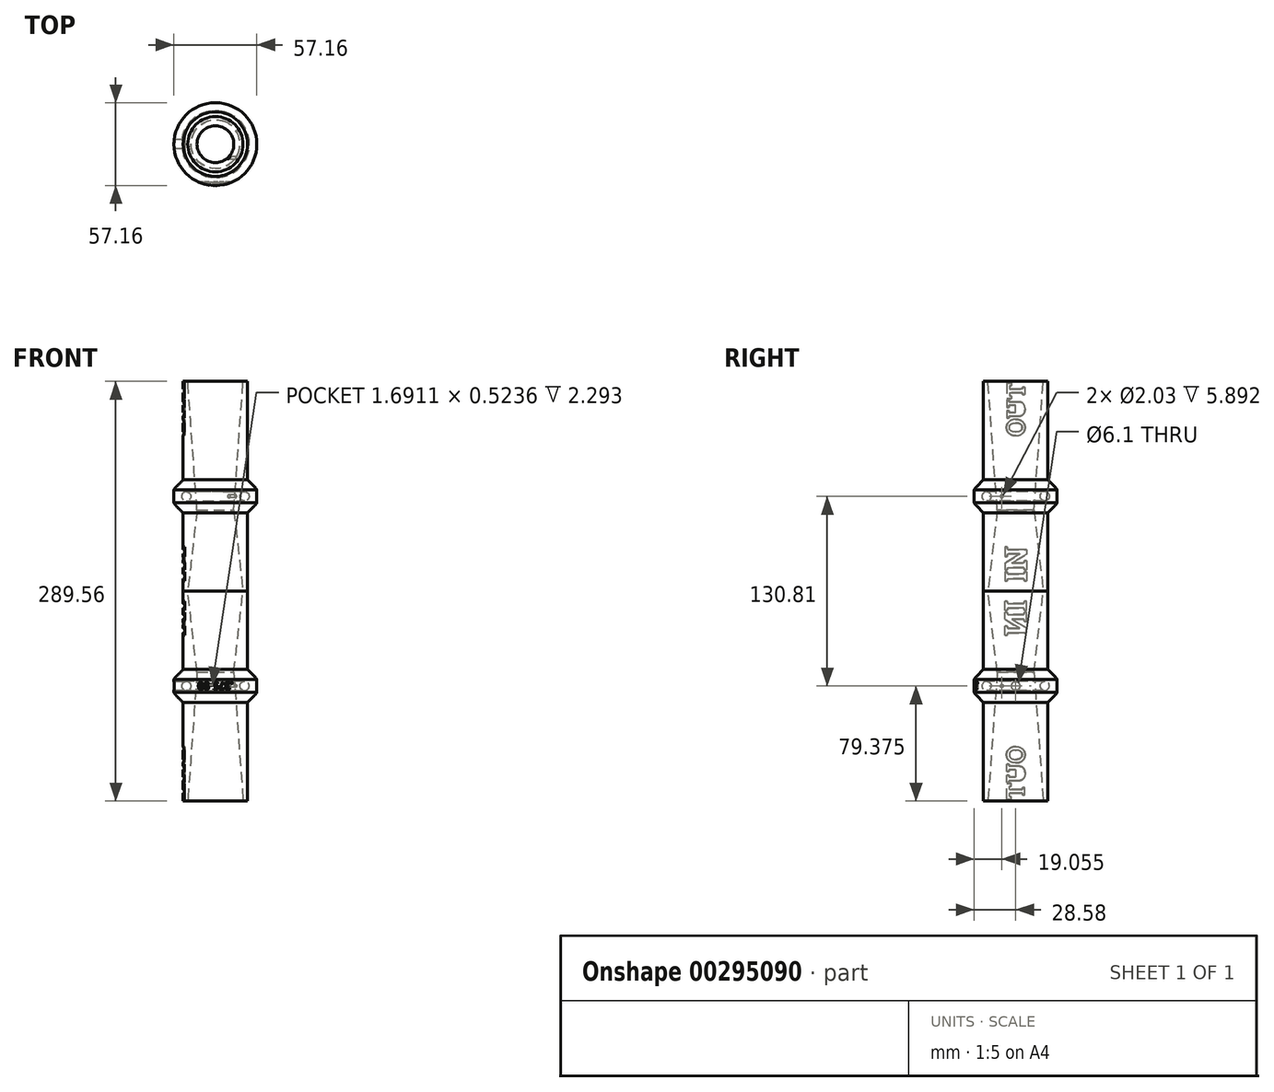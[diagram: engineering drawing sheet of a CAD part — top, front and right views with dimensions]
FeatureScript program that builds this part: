
annotation { "Feature Type Name" : "Feature", "Feature Type Description" : "" }
export const myFeature = defineFeature(function(context is Context, id is Id, definition is map)
    precondition{}
    {
        {
            var Q0;
            Q0=qCreatedBy(makeId("Front.planeOp"),FACE);
            var sketch = newSketch(context, id + "F0", { "sketchPlane" : qUnion([Q0])});
            skLineSegment(sketch, "E0", {"start": v(0, 0) * mm, "end": v(0, 144.78) * mm, "construction": true});
            skLineSegment(sketch, "E1", {"start": v(-19.05, 144.78) * mm, "end": v(-22.23, 144.78) * mm});
            skLineSegment(sketch, "E2", {"start": v(-22.23, 144.78) * mm, "end": v(-22.22, 106.68) * mm});
            skLineSegment(sketch, "E3", {"start": v(-28.58, 69.85) * mm, "end": v(-28.58, 60.96) * mm});
            skLineSegment(sketch, "E4", {"start": v(-22.23, 54) * mm, "end": v(-22.22, 0) * mm});
            skLineSegment(sketch, "E5", {"start": v(-22.22, 0) * mm, "end": v(-19.05, 0) * mm});
            skLineSegment(sketch, "E6", {"start": v(-19.05, 0) * mm, "end": v(-12.7, 55.88) * mm});
            skLineSegment(sketch, "E7", {"start": v(-12.7, 55.88) * mm, "end": v(-19.05, 144.78) * mm});
            skCircle(sketch, "E8", {"center": v(-20.1, 65.4) * mm, "radius": 3.18 * mm});
            skLineSegment(sketch, "E9", {"start": v(-22.22, 106.68) * mm, "end": v(-22.22, 76.81) * mm});
            skArc(sketch, "E10", {"start": v(-26.87, 72.17) * mm, "mid": v(-27.8, 71.08) * mm, "end": v(-28.57, 69.85) * mm});
            skPoint(sketch, "E11", {"position": v(-28.57, 69.85) * mm});
            skPoint(sketch, "E12", {"position": v(-28.57, 60.96) * mm});
            skLineSegment(sketch, "E13", {"start": v(-26.87, 58.64) * mm, "end": v(-22.23, 54) * mm});
            skLineSegment(sketch, "E14", {"start": v(-22.23, 76.81) * mm, "end": v(-26.87, 72.17) * mm});
            skArc(sketch, "E15.trimOffspring", {"start": v(-28.57, 60.96) * mm, "mid": v(-27.8, 59.73) * mm, "end": v(-26.87, 58.64) * mm});
            skLineSegment(sketch, "E16", {"start": v(-28.57, 65.4) * mm, "end": v(-11.62, 65.4) * mm, "construction": true});
            skLineSegment(sketch, "E17", {"start": v(-20.1, 65.4) * mm, "end": v(-13.38, 65.4) * mm, "construction": true});
            skSolve(sketch);
        }
        {
            var Q0;
            Q0 = qSketchRegion(id + "F0", true);
            var Q1;
            Q1=sQuery(id+"F0.wireOp",EDGE,"E0");
            revolve(context, id + "F1", {"entities" : qUnion([Q0]), "axis" : qUnion([Q1]), "revolveType" : RevolveType.FULL});
        }
        {
            var Q0;
            Q0=qCreatedBy(makeId("Right.planeOp"),FACE);
            cPlane(context, id + "F2", {"entities" : qUnion([Q0]), "cplaneType" : CPlaneType.OFFSET, "offset" : 22.22 * mm, "oppositeDirection" : true, "width" : 152.4 * mm, "height" : 152.4 * mm});
        }
        {
            var Q0;
            Q0=qCreatedBy(id+"F2.planeOp",FACE);
            var sketch = newSketch(context, id + "F3", { "sketchPlane" : qUnion([Q0])});
            skText(sketch, "E18", { "text": "IN", "fontName": "RobotoSlab-Bold.ttf"});
            skLineSegment(sketch, "E19", {"start": v(0, 0) * mm, "end": v(7.86, 1.39) * mm});
            skText(sketch, "E20", { "text": "OUT", "fontName": "RobotoSlab-Bold.ttf"});
            skLineSegment(sketch, "E21", {"start": v(0, 106.68) * mm, "end": v(0, 144.78) * mm});
            skPoint(sketch, "E22", {"position": v(0, 125.73) * mm});
            skLineSegment(sketch, "E23", {"start": v(0, 144.78) * mm, "end": v(12.99, 142.49) * mm});
            const initialGuessF3  = {"E18": [0.00786, 0.00635, 0, 1, 0.01572], "E20": [0.0063, 0.10668, 0, 1, 0.0126]};
            skSetInitialGuess(sketch, initialGuessF3);
            skSolve(sketch);
        }
        {
            var Q0;
            Q0 = qSketchRegion(id + "F3", true);
            extrude(context, id + "F4", {"entities" : qUnion([Q0]), "operationType" : NewBodyOperationType.REMOVE, "depth" : 1.27 * mm});
        }
        {
            var Q0;
            Q0=qCreatedBy(makeId("Front.planeOp"),FACE);
            cPlane(context, id + "F5", {"entities" : qUnion([Q0]), "cplaneType" : CPlaneType.OFFSET, "offset" : 9.52 * mm, "width" : 152.4 * mm, "height" : 152.4 * mm});
        }
        {
            var Q0;
            Q0=qCreatedBy(id+"F5.planeOp",FACE);
            var sketch = newSketch(context, id + "F6", { "sketchPlane" : qUnion([Q0])});
            skFitSpline(sketch, "E24", {"points": [v(-20.83, 63.9) * mm, v(-20.98, 64.2) * mm, v(-21.1, 64.52) * mm, v(-21.21, 64.95) * mm, v(-21.25, 65.4) * mm, v(-21.2, 65.84) * mm, v(-21.14, 66.17) * mm, v(-21.03, 66.49) * mm, v(-20.84, 66.89) * mm, v(-20.6, 67.26) * mm, v(-20.29, 67.59) * mm, v(-20.03, 67.8) * mm, v(-19.76, 68) * mm, v(-19.38, 68.22) * mm, v(-18.85, 68.43) * mm, v(-18.2, 68.57) * mm, v(-17.53, 68.6) * mm, v(-16.87, 68.51) * mm, v(-16.22, 68.33) * mm, v(-15.62, 68.04) * mm, v(-15.07, 67.65) * mm, v(-14.61, 67.18) * mm, v(-14.3, 66.7) * mm, v(-14.13, 66.3) * mm, v(-14, 65.87) * mm, v(-13.97, 65.42) * mm, v(-14.01, 64.98) * mm, v(-14.09, 64.65) * mm, v(-14.2, 64.34) * mm, v(-14.4, 63.93) * mm, v(-14.67, 63.57) * mm, v(-14.98, 63.25) * mm, v(-15.32, 62.97) * mm, v(-15.8, 62.67) * mm, v(-16.42, 62.41) * mm, v(-17.08, 62.26) * mm, v(-17.74, 62.21) * mm, v(-18.41, 62.27) * mm, v(-19.05, 62.44) * mm, v(-19.66, 62.73) * mm, v(-20.2, 63.12) * mm, v(-20.58, 63.54) * mm, v(-20.83, 63.9) * mm, v(-20.98, 64.2) * mm, v(-21.1, 64.52) * mm, v(-20.83, 63.9) * mm]});
            skFitSpline(sketch, "E25", {"points": [v(-21.15, 202.81) * mm, v(-20.52, 194.8) * mm, v(-19.57, 182.8) * mm, v(-18.3, 166.8) * mm, v(-17.32, 154.79) * mm, v(-16.34, 142.78) * mm, v(-15.34, 130.78) * mm, v(-14.32, 118.78) * mm, v(-13.28, 106.78) * mm, v(-12.2, 94.78) * mm, v(-11.29, 84.79) * mm, v(-10.53, 76.8) * mm, v(-9.94, 70.8) * mm, v(-9.34, 64.8) * mm, v(-8.72, 58.82) * mm, v(-8.07, 52.83) * mm, v(-7.4, 46.85) * mm, v(-6.8, 41.86) * mm, v(-6.3, 37.88) * mm, v(-5.9, 34.9) * mm, v(-5.48, 31.91) * mm, v(-5.04, 28.93) * mm, v(-4.65, 26.45) * mm, v(-4.32, 24.47) * mm, v(-4.05, 23) * mm, v(-3.78, 21.51) * mm, v(-3.48, 20.03) * mm, v(-3.16, 18.56) * mm, v(-2.87, 17.34) * mm, v(-2.62, 16.37) * mm, v(-2.42, 15.65) * mm, v(-2.2, 14.92) * mm, v(-1.96, 14.2) * mm, v(-1.7, 13.5) * mm, v(-1.44, 12.93) * mm, v(-1.2, 12.5) * mm, v(-1.01, 12.17) * mm, v(-0.78, 11.86) * mm, v(-0.55, 11.64) * mm, v(-0.33, 11.5) * mm, v(-0.15, 11.44) * mm, v(0.04, 11.42) * mm, v(0.23, 11.46) * mm, v(0.4, 11.55) * mm, v(0.62, 11.7) * mm, v(0.84, 11.93) * mm, v(1.06, 12.24) * mm, v(1.32, 12.68) * mm, v(1.59, 13.25) * mm, v(1.87, 13.95) * mm, v(2.12, 14.67) * mm, v(2.34, 15.4) * mm, v(2.62, 16.37) * mm, v(2.94, 17.6) * mm, v(3.27, 19.07) * mm, v(3.59, 20.55) * mm, v(3.88, 22.03) * mm, v(4.15, 23.52) * mm, v(4.5, 25.51) * mm, v(4.9, 28) * mm, v(5.35, 31) * mm, v(5.77, 34) * mm, v(6.18, 37) * mm, v(6.7, 41) * mm, v(7.3, 46) * mm, v(7.98, 52.02) * mm, v(8.64, 58.04) * mm, v(9.26, 64.06) * mm, v(9.87, 70.09) * mm, v(10.46, 76.12) * mm, v(11.23, 84.15) * mm, v(12.15, 94.2) * mm, v(13.23, 106.26) * mm, v(14.28, 118.33) * mm, v(15.3, 130.4) * mm, v(16.3, 142.46) * mm, v(17.3, 154.53) * mm, v(18.28, 166.6) * mm, v(19.57, 182.7) * mm, v(20.52, 194.76) * mm, v(21.15, 202.81) * mm]});
            skFitSpline(sketch, "E26", {"points": [v(-21.15, 202.81) * mm, v(-20.52, 194.8) * mm, v(-19.57, 182.8) * mm, v(-18.3, 166.8) * mm, v(-17.32, 154.79) * mm, v(-16.34, 142.78) * mm, v(-15.34, 130.78) * mm, v(-14.32, 118.78) * mm, v(-13.28, 106.78) * mm, v(-12.2, 94.78) * mm, v(-11.29, 84.79) * mm, v(-10.53, 76.8) * mm, v(-9.94, 70.8) * mm, v(-9.34, 64.8) * mm, v(-8.72, 58.82) * mm, v(-8.07, 52.83) * mm, v(-7.4, 46.85) * mm, v(-6.8, 41.86) * mm, v(-6.3, 37.88) * mm, v(-5.9, 34.9) * mm, v(-5.48, 31.91) * mm, v(-5.04, 28.93) * mm, v(-4.65, 26.45) * mm, v(-4.32, 24.47) * mm, v(-4.05, 23) * mm, v(-3.78, 21.51) * mm, v(-3.48, 20.03) * mm, v(-3.16, 18.56) * mm, v(-2.87, 17.34) * mm, v(-2.62, 16.37) * mm, v(-2.42, 15.65) * mm, v(-2.2, 14.92) * mm, v(-1.96, 14.2) * mm, v(-1.7, 13.5) * mm, v(-1.44, 12.93) * mm, v(-1.2, 12.5) * mm, v(-1.01, 12.17) * mm, v(-0.78, 11.86) * mm, v(-0.55, 11.64) * mm, v(-0.33, 11.5) * mm, v(-0.15, 11.44) * mm, v(0.04, 11.42) * mm, v(0.23, 11.46) * mm, v(0.4, 11.55) * mm, v(0.62, 11.7) * mm, v(0.84, 11.93) * mm, v(1.06, 12.24) * mm, v(1.32, 12.68) * mm, v(1.59, 13.25) * mm, v(1.87, 13.95) * mm, v(2.12, 14.67) * mm, v(2.34, 15.4) * mm, v(2.62, 16.37) * mm, v(2.94, 17.6) * mm, v(3.27, 19.07) * mm, v(3.59, 20.55) * mm, v(3.88, 22.03) * mm, v(4.15, 23.52) * mm, v(4.5, 25.51) * mm, v(4.9, 28) * mm, v(5.35, 31) * mm, v(5.77, 34) * mm, v(6.18, 37) * mm, v(6.7, 41) * mm, v(7.3, 46) * mm, v(7.98, 52.02) * mm, v(8.64, 58.04) * mm, v(9.26, 64.06) * mm, v(9.87, 70.09) * mm, v(10.46, 76.12) * mm, v(11.23, 84.15) * mm, v(12.15, 94.2) * mm, v(13.23, 106.26) * mm, v(14.28, 118.33) * mm, v(15.3, 130.4) * mm, v(16.3, 142.46) * mm, v(17.3, 154.53) * mm, v(18.28, 166.6) * mm, v(19.57, 182.7) * mm, v(20.52, 194.76) * mm, v(21.15, 202.81) * mm]});
            skFitSpline(sketch, "E27", {"points": [v(-21.15, 202.81) * mm, v(-20.52, 194.8) * mm, v(-19.57, 182.8) * mm, v(-18.3, 166.8) * mm, v(-17.32, 154.79) * mm, v(-16.34, 142.78) * mm, v(-15.34, 130.78) * mm, v(-14.32, 118.78) * mm, v(-13.28, 106.78) * mm, v(-12.2, 94.78) * mm, v(-11.29, 84.79) * mm, v(-10.53, 76.8) * mm, v(-9.94, 70.8) * mm, v(-9.34, 64.8) * mm, v(-8.72, 58.82) * mm, v(-8.07, 52.83) * mm, v(-7.4, 46.85) * mm, v(-6.8, 41.86) * mm, v(-6.3, 37.88) * mm, v(-5.9, 34.9) * mm, v(-5.48, 31.91) * mm, v(-5.04, 28.93) * mm, v(-4.65, 26.45) * mm, v(-4.32, 24.47) * mm, v(-4.05, 23) * mm, v(-3.78, 21.51) * mm, v(-3.48, 20.03) * mm, v(-3.16, 18.56) * mm, v(-2.87, 17.34) * mm, v(-2.62, 16.37) * mm, v(-2.42, 15.65) * mm, v(-2.2, 14.92) * mm, v(-1.96, 14.2) * mm, v(-1.7, 13.5) * mm, v(-1.44, 12.93) * mm, v(-1.2, 12.5) * mm, v(-1.01, 12.17) * mm, v(-0.78, 11.86) * mm, v(-0.55, 11.64) * mm, v(-0.33, 11.5) * mm, v(-0.15, 11.44) * mm, v(0.04, 11.42) * mm, v(0.23, 11.46) * mm, v(0.4, 11.55) * mm, v(0.62, 11.7) * mm, v(0.84, 11.93) * mm, v(1.06, 12.24) * mm, v(1.32, 12.68) * mm, v(1.59, 13.25) * mm, v(1.87, 13.95) * mm, v(2.12, 14.67) * mm, v(2.34, 15.4) * mm, v(2.62, 16.37) * mm, v(2.94, 17.6) * mm, v(3.27, 19.07) * mm, v(3.59, 20.55) * mm, v(3.88, 22.03) * mm, v(4.15, 23.52) * mm, v(4.5, 25.51) * mm, v(4.9, 28) * mm, v(5.35, 31) * mm, v(5.77, 34) * mm, v(6.18, 37) * mm, v(6.7, 41) * mm, v(7.3, 46) * mm, v(7.98, 52.02) * mm, v(8.64, 58.04) * mm, v(9.26, 64.06) * mm, v(9.87, 70.09) * mm, v(10.46, 76.12) * mm, v(11.23, 84.15) * mm, v(12.15, 94.2) * mm, v(13.23, 106.26) * mm, v(14.28, 118.33) * mm, v(15.3, 130.4) * mm, v(16.3, 142.46) * mm, v(17.3, 154.53) * mm, v(18.28, 166.6) * mm, v(19.57, 182.7) * mm, v(20.52, 194.76) * mm, v(21.15, 202.81) * mm]});
            skFitSpline(sketch, "E28", {"points": [v(-20.83, 63.9) * mm, v(-20.98, 64.2) * mm, v(-21.1, 64.52) * mm, v(-21.21, 64.95) * mm, v(-21.25, 65.4) * mm, v(-21.2, 65.84) * mm, v(-21.14, 66.17) * mm, v(-21.03, 66.49) * mm, v(-20.84, 66.89) * mm, v(-20.6, 67.26) * mm, v(-20.29, 67.59) * mm, v(-20.03, 67.8) * mm, v(-19.76, 68) * mm, v(-19.38, 68.22) * mm, v(-18.85, 68.43) * mm, v(-18.2, 68.57) * mm, v(-17.53, 68.6) * mm, v(-16.87, 68.51) * mm, v(-16.22, 68.33) * mm, v(-15.62, 68.04) * mm, v(-15.07, 67.65) * mm, v(-14.61, 67.18) * mm, v(-14.3, 66.7) * mm, v(-14.13, 66.3) * mm, v(-14, 65.87) * mm, v(-13.97, 65.42) * mm, v(-14.01, 64.98) * mm, v(-14.09, 64.65) * mm, v(-14.2, 64.34) * mm, v(-14.4, 63.93) * mm, v(-14.67, 63.57) * mm, v(-14.98, 63.25) * mm, v(-15.32, 62.97) * mm, v(-15.8, 62.67) * mm, v(-16.42, 62.41) * mm, v(-17.08, 62.26) * mm, v(-17.74, 62.21) * mm, v(-18.41, 62.27) * mm, v(-19.05, 62.44) * mm, v(-19.66, 62.73) * mm, v(-20.2, 63.12) * mm, v(-20.58, 63.54) * mm, v(-20.83, 63.9) * mm, v(-20.98, 64.2) * mm, v(-21.1, 64.52) * mm, v(-20.83, 63.9) * mm]});
            skFitSpline(sketch, "E29", {"points": [v(14.34, 64.06) * mm, v(14.14, 64.46) * mm, v(14.02, 64.9) * mm, v(13.98, 65.34) * mm, v(14, 65.67) * mm, v(14.05, 66) * mm, v(14.14, 66.33) * mm, v(14.28, 66.63) * mm, v(14.44, 66.92) * mm, v(14.64, 67.2) * mm, v(14.94, 67.52) * mm, v(15.37, 67.88) * mm, v(15.85, 68.16) * mm, v(16.27, 68.33) * mm, v(16.7, 68.47) * mm, v(17.13, 68.55) * mm, v(17.57, 68.58) * mm, v(18.02, 68.58) * mm, v(18.45, 68.52) * mm, v(18.89, 68.4) * mm, v(19.3, 68.25) * mm, v(19.7, 68.05) * mm, v(20.06, 67.78) * mm, v(20.3, 67.56) * mm, v(20.53, 67.32) * mm, v(20.73, 67.05) * mm, v(20.9, 66.76) * mm, v(21.04, 66.46) * mm, v(21.14, 66.14) * mm, v(21.23, 65.7) * mm, v(21.24, 65.26) * mm, v(21.18, 64.81) * mm, v(21.1, 64.49) * mm, v(20.97, 64.18) * mm, v(20.76, 63.78) * mm, v(20.5, 63.43) * mm, v(20.17, 63.11) * mm, v(19.9, 62.9) * mm, v(19.62, 62.73) * mm, v(19.22, 62.52) * mm, v(18.7, 62.34) * mm, v(18.03, 62.23) * mm, v(17.37, 62.22) * mm, v(16.7, 62.33) * mm, v(16.07, 62.54) * mm, v(15.48, 62.86) * mm, v(15.04, 63.2) * mm, v(14.73, 63.51) * mm, v(14.52, 63.78) * mm, v(14.34, 64.06) * mm, v(14.14, 64.46) * mm, v(14.02, 64.9) * mm, v(14.34, 64.06) * mm]});
            skLineSegment(sketch, "E30", {"start": v(21.23, 65.4) * mm, "end": v(13.99, 65.4) * mm, "construction": true});
            skLineSegment(sketch, "E31", {"start": v(17.6, 68.58) * mm, "end": v(17.6, 62.23) * mm, "construction": true});
            skPoint(sketch, "E32", {"position": v(17.6, 65.4) * mm});
            skLineSegment(sketch, "E33", {"start": v(17.6, 65.4) * mm, "end": v(9.4, 65.4) * mm});
            skLineSegment(sketch, "E34", {"start": v(9.4, 65.4) * mm, "end": v(8.74, 65.4) * mm});
            skLineSegment(sketch, "E35", {"start": v(9.5, 66.42) * mm, "end": v(17.6, 66.42) * mm});
            skLineSegment(sketch, "E36", {"start": v(17.6, 66.42) * mm, "end": v(17.6, 65.4) * mm});
            skLineSegment(sketch, "E37", {"start": v(9.5, 66.42) * mm, "end": v(8.74, 66.42) * mm});
            skLineSegment(sketch, "E38", {"start": v(8.74, 66.42) * mm, "end": v(8.74, 65.4) * mm});
            skSolve(sketch);
        }
        {
            var Q0;
            {var subQ0=sQuery(id+"F6.wireOp",EDGE,"E33");var subQ5=sQuery(id+"F6.wireOp",EDGE,"E29");var subQ6=makeQuery(id+"F6.imprint","INTERSECT",VERTEX,{"derivedFrom":[subQ5,subQ0]});Q0=makeQuery(id+"F6.imprint","IMPRINT",FACE,{"disambiguationData":[TD([[makeQuery(id+"F6.imprint","IMPRINT",EDGE,{"disambiguationData":[TD([[subQ6,-1.0]])],"derivedFrom":subQ5}),1.0]])]});}
            var Q1;
            {var subQ5=sQuery(id+"F6.wireOp",EDGE,"E36");Q1=makeQuery(id+"F6.imprint","IMPRINT",FACE,{"disambiguationData":[TD([[makeQuery(id+"F6.imprint","IMPRINT",EDGE,{"derivedFrom":subQ5}),-1.0]])]});}
            var Q2;
            {var subQ0=sQuery(id+"F6.wireOp",EDGE,"E34");Q2=makeQuery(id+"F6.imprint","IMPRINT",FACE,{"disambiguationData":[TD([[makeQuery(id+"F6.imprint","IMPRINT",EDGE,{"derivedFrom":subQ0}),-1.0]])]});}
            var Q3;
            Q3=sQuery(id+"F6.wireOp",EDGE,"E34");
            revolve(context, id + "F7", {"operationType" : NewBodyOperationType.REMOVE, "entities" : qUnion([Q0, Q1, Q2]), "axis" : qUnion([Q3]), "revolveType" : RevolveType.FULL, "oppositeDirection" : true});
        }
        {
            var Q0;
            Q0=makeQuery(id+"F1.opRevolve","SWEPT_BODY",BODY,{"disambiguationData":[OSD([sQuery(id+"F0.wireOp",EDGE,"E1"),sQuery(id+"F0.wireOp",EDGE,"E2"),sQuery(id+"F0.wireOp",EDGE,"xNmsN8NY-gJYZ-bOfs-Yh8i-QKWzSkXoU7w8"),sQuery(id+"F0.wireOp",EDGE,"E3"),sQuery(id+"F0.wireOp",EDGE,"PNRozeE3-dEe6-HTJB-bdQW-iLLAFMeGhy6S"),sQuery(id+"F0.wireOp",EDGE,"E4"),sQuery(id+"F0.wireOp",EDGE,"E5"),sQuery(id+"F0.wireOp",EDGE,"E6"),sQuery(id+"F0.wireOp",EDGE,"E7")])]});
            var Q1;
            Q1=makeQuery(id+"F1.opRevolve","SWEPT_FACE",FACE,{"disambiguationData":[OSD([sQuery(id+"F0.wireOp",EDGE,"E5")])]});
            mirror(context, id + "F8", {"entities" : qUnion([Q0]), "mirrorPlane" : qUnion([Q1])});
        }
        {
            var Q0;
            Q0=qCreatedBy(makeId("Front.planeOp"),FACE);
            var sketch = newSketch(context, id + "F9", { "sketchPlane" : qUnion([Q0])});
            skCircle(sketch, "E39", {"center": v(20.1, -65.4) * mm, "radius": 3.18 * mm});
            skCircle(sketch, "E40", {"center": v(-20.1, -65.4) * mm, "radius": 3.18 * mm});
            skLineSegment(sketch, "E41", {"start": v(-20.1, -65.4) * mm, "end": v(-30.26, -65.4) * mm});
            skLineSegment(sketch, "E42", {"start": v(-30.26, -65.4) * mm, "end": v(-30.26, -62.36) * mm});
            skLineSegment(sketch, "E43", {"start": v(-30.26, -62.36) * mm, "end": v(-20.1, -62.36) * mm});
            skLineSegment(sketch, "E44", {"start": v(-20.1, -62.36) * mm, "end": v(-20.1, -65.4) * mm});
            skLineSegment(sketch, "E45", {"start": v(-20.1, -63.88) * mm, "end": v(-21.62, -62.36) * mm});
            skSolve(sketch);
        }
        {
            var Q0;
            {var subQ0=sQuery(id+"F9.wireOp",EDGE,"E41");var subQ1=sQuery(id+"F9.wireOp",EDGE,"E40");var subQ2=makeQuery(id+"F9.imprint","INTERSECT",VERTEX,{"derivedFrom":[subQ1,subQ0]});Q0=makeQuery(id+"F9.imprint","IMPRINT",FACE,{"disambiguationData":[TD([[makeQuery(id+"F9.imprint","IMPRINT",EDGE,{"disambiguationData":[TD([[subQ2,-1.0]])],"derivedFrom":subQ1}),-1.0]])]});}
            var Q1;
            {var subQ1=sQuery(id+"F9.wireOp",EDGE,"E42");Q1=makeQuery(id+"F9.imprint","IMPRINT",FACE,{"disambiguationData":[TD([[makeQuery(id+"F9.imprint","IMPRINT",EDGE,{"derivedFrom":subQ1}),-1.0]])]});}
            var Q2;
            Q2=sQuery(id+"F9.wireOp",EDGE,"E41");
            revolve(context, id + "F10", {"operationType" : NewBodyOperationType.REMOVE, "entities" : qUnion([Q0, Q1]), "axis" : qUnion([Q2]), "revolveType" : RevolveType.FULL, "oppositeDirection" : true});
        }
        {
            var Q0;
            Q0=qCreatedBy(makeId("Front.planeOp"),FACE);
            cPlane(context, id + "F11", {"entities" : qUnion([Q0]), "cplaneType" : CPlaneType.OFFSET, "offset" : 28.57 * mm, "width" : 152.4 * mm, "height" : 152.4 * mm});
        }
        {
            var Q0;
            Q0=qCreatedBy(id+"F11.planeOp",FACE);
            var sketch = newSketch(context, id + "F12", { "sketchPlane" : qUnion([Q0])});
            skText(sketch, "E46", { "text": ".375-00", "fontName": "OpenSans-Regular.ttf"});
            skLineSegment(sketch, "E47.0", {"start": v(28.57, -69.85) * mm, "end": v(-28.57, -69.85) * mm});
            skLineSegment(sketch, "E48.0", {"start": v(28.58, -60.96) * mm, "end": v(-28.58, -60.96) * mm});
            skLineSegment(sketch, "E49", {"start": v(0, -69.85) * mm, "end": v(0, -60.96) * mm});
            skPoint(sketch, "E50", {"position": v(0, -65.4) * mm});
            const initialGuessF12  = {"E46": [0.01221, -0.06287, -1, 0, 0.00508]};
            skSetInitialGuess(sketch, initialGuessF12);
            skSolve(sketch);
        }
        {
            var Q0;
            Q0 = qSketchRegion(id + "F12", true);
            extrude(context, id + "F13", {"entities" : qUnion([Q0]), "operationType" : NewBodyOperationType.REMOVE, "oppositeDirection" : true, "depth" : 2.54 * mm});
        }
    });
